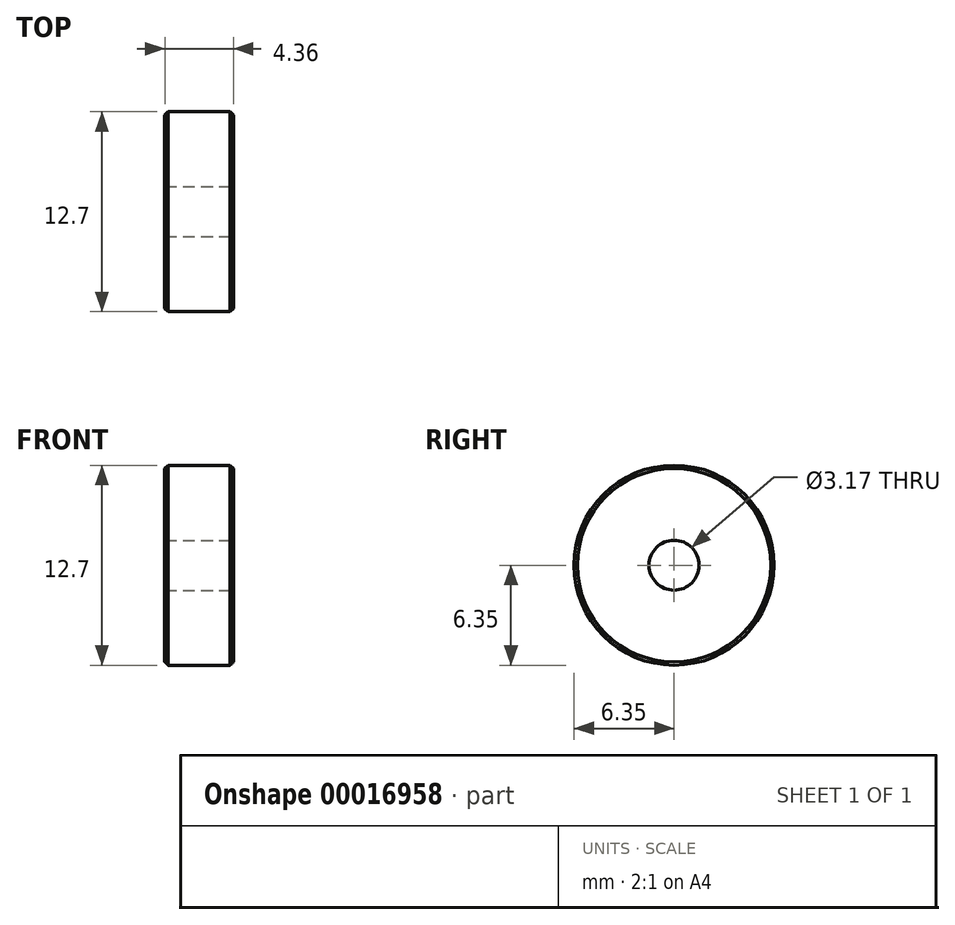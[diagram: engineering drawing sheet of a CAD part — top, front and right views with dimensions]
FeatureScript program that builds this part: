
annotation { "Feature Type Name" : "Feature", "Feature Type Description" : "" }
export const myFeature = defineFeature(function(context is Context, id is Id, definition is map)
    precondition{}
    {
        {
            var Q0;
            Q0=qCreatedBy(makeId("Front.planeOp"),FACE);
            var sketch = newSketch(context, id + "F0", { "sketchPlane" : qUnion([Q0])});
            skLineSegment(sketch, "E0", {"start": v(0, 0) * mm, "end": v(-2.6, 0) * mm, "construction": true});
            skLineSegment(sketch, "E1", {"start": v(0, 0) * mm, "end": v(0, 2.95) * mm, "construction": true});
            skLineSegment(sketch, "E2", {"start": v(0, 1.59) * mm, "end": v(-2.18, 1.59) * mm});
            skLineSegment(sketch, "E3", {"start": v(-2.18, 1.59) * mm, "end": v(-2.18, 6.14) * mm});
            skLineSegment(sketch, "E4", {"start": v(-1.96, 6.35) * mm, "end": v(0, 6.35) * mm});
            skLineSegment(sketch, "E5", {"start": v(-2.18, 6.14) * mm, "end": v(-1.96, 6.35) * mm});
            skLineSegment(sketch, "E6.MirrorCS", {"start": v(0, 1.59) * mm, "end": v(2.18, 1.59) * mm});
            skLineSegment(sketch, "E7.MirrorCS", {"start": v(2.18, 1.59) * mm, "end": v(2.18, 6.14) * mm});
            skLineSegment(sketch, "E8.MirrorCS", {"start": v(2.18, 6.14) * mm, "end": v(1.96, 6.35) * mm});
            skLineSegment(sketch, "E9.MirrorCS", {"start": v(1.96, 6.35) * mm, "end": v(0, 6.35) * mm});
            skSolve(sketch);
        }
        {
            var Q0;
            Q0=makeQuery(id+"F0.imprint","IMPRINT",FACE,{"disambiguationData":[TD([[makeQuery(id+"F0.imprint","IMPRINT",EDGE,{"derivedFrom":sQuery(id+"F0.wireOp",EDGE,"E2")}),-1.0]])]});
            var Q1;
            Q1=sQuery(id+"F0.wireOp",EDGE,"E0");
            revolve(context, id + "F1", {"entities" : qUnion([Q0]), "axis" : qUnion([Q1]), "revolveType" : RevolveType.FULL});
        }
    });
